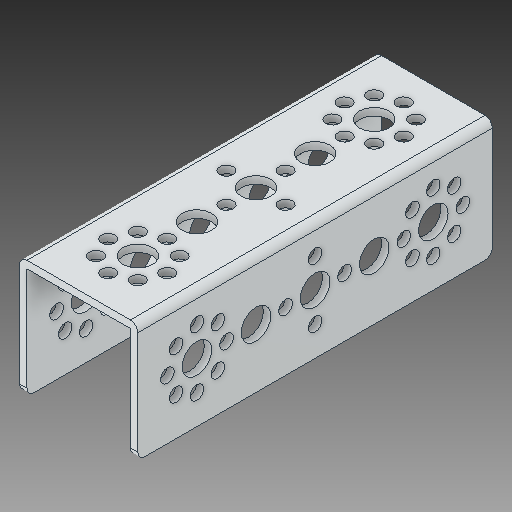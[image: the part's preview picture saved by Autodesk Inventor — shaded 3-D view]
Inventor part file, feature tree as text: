
AUTODESK INVENTOR PART (.ipt)
format: ipt  version: 2018 (Build 220112000, 112)  size: 301,056 bytes
history: native  units: in
note: dims shown in document units (in); Inventor stores cm internally (conversion verified against a paired STEP export)
features: fillet x1
ambient origin geometry x8: Origin, YZ Plane, XZ Plane, XY Plane, X Axis, Y Axis, Z Axis, Center Point
bodies: Solid1 (feature_tree)
feature tree (1):
  fillet  "Fillet1"  [1 undecoded]
note: 1 required parameter value undecoded (feature->parameter linkage not recoverable at this tier; creation-order binding heuristic only, values carry confidence <= 0.55)
